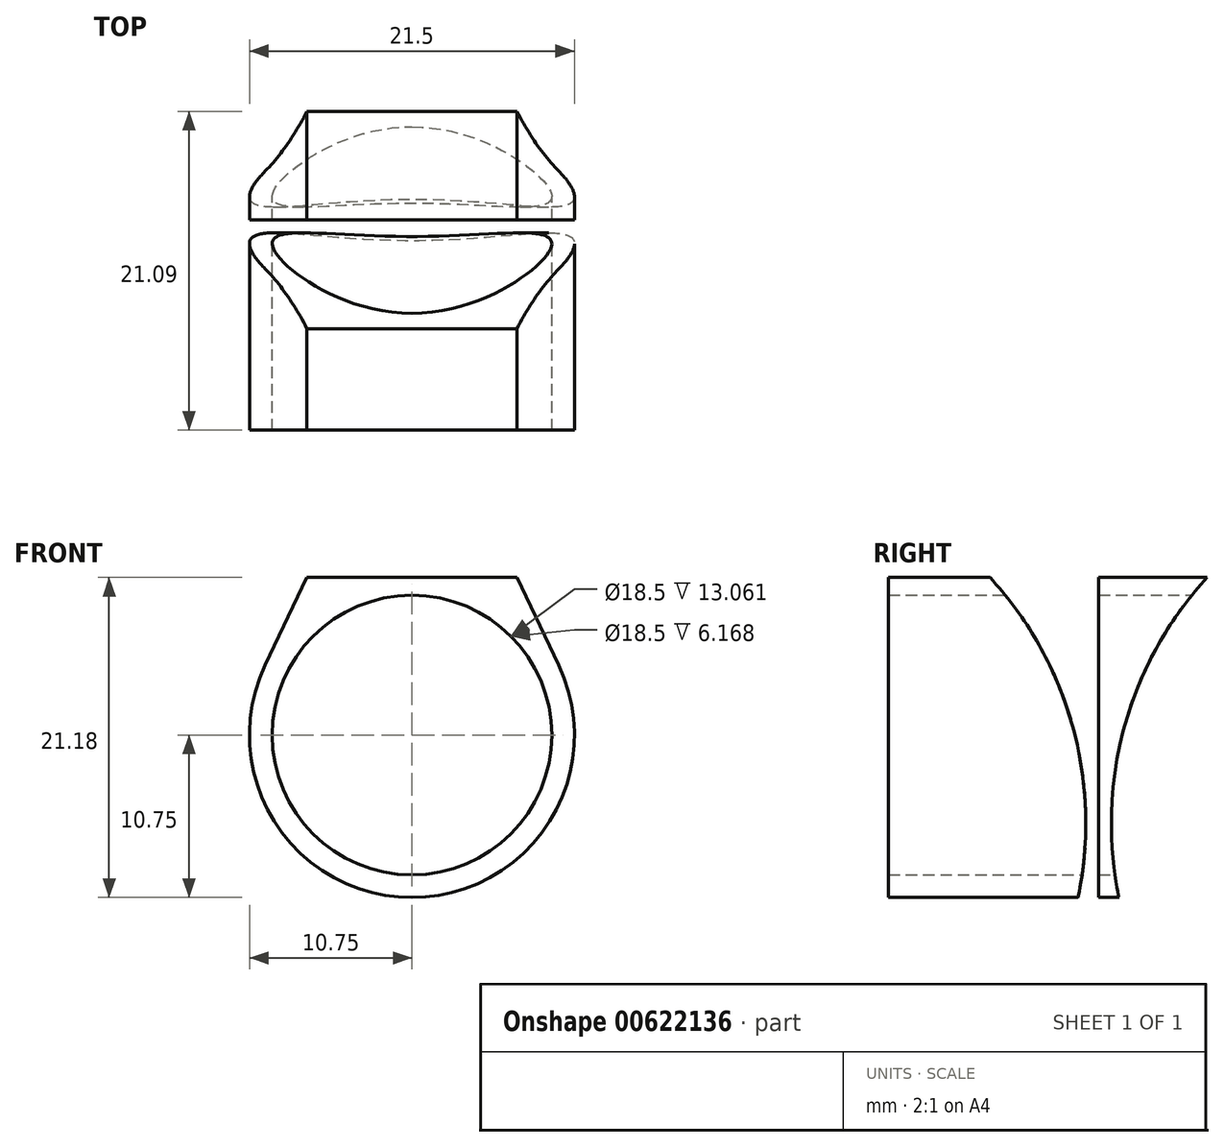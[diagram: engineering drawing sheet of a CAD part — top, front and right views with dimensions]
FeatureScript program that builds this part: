
annotation { "Feature Type Name" : "Feature", "Feature Type Description" : "" }
export const myFeature = defineFeature(function(context is Context, id is Id, definition is map)
    precondition{}
    {
        {
            var Q0;
            Q0=qCreatedBy(makeId("Front.planeOp"),FACE);
            var sketch = newSketch(context, id + "F0", { "sketchPlane" : qUnion([Q0])});
            skCircle(sketch, "E0", {"center": v(0, 0) * mm, "radius": 9.25 * mm});
            skArc(sketch, "E1", {"start": v(-9.7, 4.61) * mm, "mid": v(0, -10.75) * mm, "end": v(9.7, 4.61) * mm});
            skLineSegment(sketch, "E2", {"start": v(-2.59, 10.43) * mm, "end": v(2.59, 10.43) * mm});
            skLineSegment(sketch, "E3", {"start": v(2.59, 10.43) * mm, "end": v(6.94, 10.43) * mm});
            skLineSegment(sketch, "E4", {"start": v(6.94, 10.43) * mm, "end": v(9.7, 4.61) * mm});
            skLineSegment(sketch, "E5.MirrorCS", {"start": v(-6.94, 10.43) * mm, "end": v(-9.7, 4.61) * mm});
            skLineSegment(sketch, "E6.MirrorCS", {"start": v(-2.59, 10.43) * mm, "end": v(-6.94, 10.43) * mm});
            skSolve(sketch);
        }
        {
            var Q0;
            Q0=makeQuery(id+"F0.imprint","IMPRINT",FACE,{"disambiguationData":[TD([[makeQuery(id+"F0.imprint","IMPRINT",EDGE,{"derivedFrom":sQuery(id+"F0.wireOp",EDGE,"E0")}),-1.0]])]});
            extrude(context, id + "F1", {"entities" : qUnion([Q0]), "depth" : 25.4 * mm, "offsetDistance" : 25.4 * mm});
        }
        {
            var Q0;
            Q0=qCreatedBy(makeId("Right.planeOp"),FACE);
            var sketch = newSketch(context, id + "F2", { "sketchPlane" : qUnion([Q0])});
            skArc(sketch, "E7", {"start": v(-3.54, 11.23) * mm, "mid": v(-9.66, 0.98) * mm, "end": v(-10.1, -10.94) * mm});
            skLineSegment(sketch, "E8", {"start": v(-3.54, 11.23) * mm, "end": v(-11.5, 11.23) * mm});
            skLineSegment(sketch, "E9", {"start": v(-11.5, 11.23) * mm, "end": v(-11.5, -10.94) * mm});
            skLineSegment(sketch, "E10", {"start": v(-11.5, -10.94) * mm, "end": v(-10.1, -10.94) * mm});
            skLineSegment(sketch, "E11.MirrorCS", {"start": v(-19.45, 11.23) * mm, "end": v(-11.5, 11.23) * mm});
            skArc(sketch, "E12.MirrorCS", {"start": v(-19.45, 11.23) * mm, "mid": v(-13.33, 0.98) * mm, "end": v(-12.89, -10.94) * mm});
            skLineSegment(sketch, "E13.MirrorCS", {"start": v(-11.5, -10.94) * mm, "end": v(-12.89, -10.94) * mm});
            skLineSegment(sketch, "E14", {"start": v(-19.45, 11.23) * mm, "end": v(-29.9, 11.23) * mm});
            skLineSegment(sketch, "E15", {"start": v(-29.9, 11.23) * mm, "end": v(-28.96, -13.81) * mm});
            skLineSegment(sketch, "E16", {"start": v(-28.96, -13.81) * mm, "end": v(-12.89, -10.94) * mm});
            skLineSegment(sketch, "E17.MirrorCS", {"start": v(-3.54, 11.23) * mm, "end": v(6.9, 11.23) * mm});
            skLineSegment(sketch, "E18.MirrorCS", {"start": v(6.9, 11.23) * mm, "end": v(5.97, -13.81) * mm});
            skLineSegment(sketch, "E19.MirrorCS", {"start": v(5.97, -13.81) * mm, "end": v(-10.1, -10.94) * mm});
            skSolve(sketch);
        }
        {
            var Q0;
            Q0=makeQuery(id+"F2.imprint","IMPRINT",FACE,{"disambiguationData":[TD([[makeQuery(id+"F2.imprint","IMPRINT",EDGE,{"derivedFrom":sQuery(id+"F2.wireOp",EDGE,"E12.MirrorCS")}),-1.0]])]});
            var Q1;
            Q1=makeQuery(id+"F2.imprint","IMPRINT",FACE,{"disambiguationData":[TD([[makeQuery(id+"F2.imprint","IMPRINT",EDGE,{"derivedFrom":sQuery(id+"F2.wireOp",EDGE,"E7")}),1.0]])]});
            extrude(context, id + "F3", {"entities" : qUnion([Q0, Q1]), "operationType" : NewBodyOperationType.REMOVE, "endBound" : BoundingType.SYMMETRIC, "depth" : 25.4 * mm, "offsetDistance" : 25.4 * mm});
        }
    });
